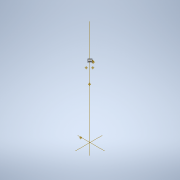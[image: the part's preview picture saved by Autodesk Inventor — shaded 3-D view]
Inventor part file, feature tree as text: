
AUTODESK INVENTOR PART (.ipt)
format: ipt  version: 2021 (Build 250183000, 183)  size: 13,105,664 bytes
history: native  units: mm
features: sketch x88, fillet x71, extrude x63, other x21, plane x15, revolve x12, pattern_circular x10, sweep x6, mirror x2, chamfer x1
ambient origin geometry x8: Origin, YZ Plane, XZ Plane, XY Plane, X Axis, Y Axis, Z Axis, Center Point
bodies: Body1 (feature_tree), Body2 (feature_tree), Body3 (feature_tree), Body4 (feature_tree), Body5 (feature_tree), Body6 (feature_tree), Body7 (feature_tree), Body8 (feature_tree), Body9 (feature_tree), Body10 (feature_tree), Body11 (feature_tree), Body12 (feature_tree)
feature tree (289):
  other  "Soyuz Core Stage"
  extrude  "Core Airframe"  Depth=133.0mm TaperAngle=0.0deg
  extrude  "Vernier Housing"  Depth=3.4mm
  extrude  "Main Engine Extrude"  TaperAngle=0.0deg  [1 undecoded]
  extrude  "Main Engine Cut"  Depth=3.4mm
  extrude  "Vernier Nozzels"  Depth=3.4mm
  extrude  "Extrusion11"  Depth=3.4mm
  extrude  "Extrusion12"  Depth=5.5mm
  sweep  "Sweep1"
  sweep  "Booster Nosecone"
  extrude  "Extrusion16"  Depth=4.5mm
  plane  "Work Plane6"
  extrude  "Extrusion17"  Depth=4.5mm
  plane  "Work Plane5"
  extrude  "Extrusion18"  Depth=4.5mm
  fillet  "Fillet11"  Radius=4.5mm
  fillet  "Fillet12"  Radius=6.0mm
  fillet  "Fillet13"  Radius=2.0mm
  fillet  "Fillet14"  Radius=10.5mm
  extrude  "Booster Lock Extrusion"  Depth=2.0mm
  extrude  "Booster Lock Cut"  Depth=10.5mm
  other  "Work Point1"
  plane  "Work Plane1"
  sweep  "Sweep4"
  extrude  "Extrusion26"  TaperAngle=0.0deg  [1 undecoded]
  fillet  "Fillet16"  [1 undecoded]
  plane  "Work Plane4"
  other  "Work Point2"
  plane  "Work Plane2"
  extrude  "Extrusion27"  Depth=5.0mm
  extrude  "Extrusion28"  Depth=5.0mm
  extrude  "Extrusion29"  Depth=5.0mm
  fillet  "Fillet17"  [1 undecoded]
  fillet  "Fillet18"  [1 undecoded]
  fillet  "Fillet19"  [1 undecoded]
  extrude  "Extrusion30"  Depth=9.0mm
  fillet  "Fillet20"  Radius=28.0mm
  fillet  "Fillet21"  Radius=25.0mm
  fillet  "Fillet22"  [1 undecoded]
  extrude  "Extrusion31"  Depth=13.0mm
  extrude  "Extrusion32"  TaperAngle=0.0deg  [1 undecoded]
  extrude  "Extrusion33"  TaperAngle=0.0deg  [1 undecoded]
  extrude  "Extrusion34"  TaperAngle=0.0deg  [1 undecoded]
  fillet  "Fillet23"  [1 undecoded]
  fillet  "Fillet24"  Radius=17.0mm
  fillet  "Fillet25"  Radius=23.0mm
  fillet  "Fillet26"  [1 undecoded]
  extrude  "Extrusion35"  TaperAngle=0.0deg  [1 undecoded]
  extrude  "Extrusion36"  Depth=15.0mm
  extrude  "Extrusion50"  Depth=1.5mm
  fillet  "Fillet75"  [1 undecoded]
  extrude  "Extrusion51"  Depth=3.0mm TaperAngle=0.0deg
  extrude  "Extrusion52"  Depth=0.5mm TaperAngle=0.0deg
  other  "Work Point13"
  sketch  "Sketch86"  dims[d351=0.0mm]
  sweep  "Sweep6"
  revolve  "Revolution2"  [1 undecoded]
  pattern_circular  "Circular Pattern5"  [2 undecoded]
  mirror  "Mirror4"
  revolve  "Revolution3"  [1 undecoded]
  fillet  "Fillet76"  Radius=1.0mm
  fillet  "Fillet77"  Radius=6.0mm
  fillet  "Fillet78"  [1 undecoded]
  fillet  "Fillet79"  [1 undecoded]
  fillet  "Fillet80"  Radius=5.0mm
  fillet  "Fillet81"  Radius=2.0mm
  fillet  "Fillet82"  Radius=2.0mm
  fillet  "Fillet83"  [1 undecoded]
  fillet  "Fillet84"  Radius=10.0mm
  fillet  "Fillet85"  Radius=0.5mm
  fillet  "Fillet86"  Radius=3.0mm
  extrude  "Extrusion54"  Depth=1.0mm
  fillet  "Fillet91"  Radius=1.0mm
  fillet  "Fillet92"  Radius=28.0mm
  fillet  "Fillet93"  Radius=0.5mm
  pattern_circular  "Circular Pattern6"  [2 undecoded]
  plane  "Work Plane20"
  extrude  "Extrusion56"  TaperAngle=0.0deg  [1 undecoded]
  pattern_circular  "Circular Pattern8"  [2 undecoded]
  extrude  "Extrusion57"  TaperAngle=0.0deg  [1 undecoded]
  extrude  "Extrusion58"  Depth=0.5mm TaperAngle=0.0deg
  fillet  "Fillet94"  Radius=3.0mm
  extrude  "Extrusion59"  Depth=0.5mm
  fillet  "Fillet95"  Radius=0.1mm
  pattern_circular  "Circular Pattern9"  Count=2  [1 undecoded]
  extrude  "Extrusion60"  Depth=0.5mm TaperAngle=0.0deg
  fillet  "Fillet96"  [1 undecoded]
  extrude  "Extrusion61"  TaperAngle=0.0deg  [1 undecoded]
  fillet  "Fillet97"  [1 undecoded]
  extrude  "Extrusion62"  TaperAngle=0.0deg  [1 undecoded]
  pattern_circular  "Circular Pattern11"  [2 undecoded]
  fillet  "Fillet98"  [1 undecoded]
  extrude  "Extrusion63"  TaperAngle=0.0deg  [1 undecoded]
  fillet  "Fillet99"  [1 undecoded]
  fillet  "Fillet100"  [1 undecoded]
  extrude  "Extrusion64"  TaperAngle=0.0deg  [1 undecoded]
  extrude  "Extrusion65"  TaperAngle=0.0deg  [1 undecoded]
  extrude  "Extrusion66"  TaperAngle=0.0deg  [1 undecoded]
  extrude  "Extrusion67"  Depth=0.5mm
  fillet  "Fillet101"  Radius=12.5mm
  plane  "Work Plane24"
  extrude  "Extrusion68"  Depth=0.5mm
  fillet  "Fillet102"  Radius=12.5mm
  extrude  "Extrusion69"  TaperAngle=0.0deg  [1 undecoded]
  pattern_circular  "Circular Pattern12"  [2 undecoded]
  extrude  "Extrusion70"  TaperAngle=0.0deg  [1 undecoded]
  fillet  "Fillet103"  [1 undecoded]
  pattern_circular  "Circular Pattern13"  [2 undecoded]
  extrude  "Extrusion71"  TaperAngle=0.0deg  [1 undecoded]
  extrude  "Extrusion72"  TaperAngle=0.0deg  [1 undecoded]
  extrude  "Extrusion73"  TaperAngle=0.0deg  [1 undecoded]
  fillet  "Fillet105"  [1 undecoded]
  extrude  "Extrusion74"  TaperAngle=0.0deg  [1 undecoded]
  extrude  "Extrusion75"  TaperAngle=0.0deg  [1 undecoded]
  fillet  "Fillet106"  [1 undecoded]
  fillet  "Fillet107"  Radius=6.0mm
  other  "Work Point16"
  revolve  "Revolution6"  [1 undecoded]
  other  "Work Point17"
  plane  "Work Plane26"
  extrude  "Extrusion81"  Depth=0.5mm
  fillet  "Fillet114"  Radius=6.0mm
  fillet  "Fillet115"  [1 undecoded]
  fillet  "Fillet116"  [1 undecoded]
  fillet  "Fillet117"  Radius=5.0mm
  mirror  "Mirror6"
  sweep  "Sweep8"
  pattern_circular  "Circular Pattern14"  [2 undecoded]
  extrude  "Extrusion80"  Depth=0.5mm
  revolve  "Revolution5"  [1 undecoded]
  extrude  "Extrusion82"  Depth=1.0mm
  fillet  "Fillet118"  [1 undecoded]
  other  "Work Point18"
  plane  "Work Plane27"
  extrude  "Extrusion83"  Depth=0.5mm
  sweep  "Sweep9"
  revolve  "Revolution7"  [1 undecoded]
  revolve  "Revolution8"  [1 undecoded]
  revolve  "Revolution9"  [1 undecoded]
  revolve  "Revolution10"  [1 undecoded]
  fillet  "Fillet119"  Radius=0.781667mm
  fillet  "Fillet120"  Radius=2.5mm
  fillet  "Fillet121"  Radius=12.5mm
  fillet  "Fillet122"  Radius=12.5mm
  fillet  "Fillet123"  Radius=0.5mm
  fillet  "Fillet124"  [1 undecoded]
  plane  "Work Plane30"
  extrude  "Extrusion85"  Depth=0.5mm
  extrude  "Extrusion86"  Depth=0.5mm
  extrude  "Extrusion87"  Depth=0.5mm
  extrude  "Extrusion88"  TaperAngle=0.0deg  [1 undecoded]
  fillet  "Fillet125"  Radius=1.0mm
  fillet  "Fillet126"  Radius=1.377412mm
  fillet  "Fillet127"  Radius=1.377mm
  fillet  "Fillet128"  Radius=4.5mm
  extrude  "Extrusion89"  Depth=1.0mm
  extrude  "Extrusion90"  Depth=0.5mm TaperAngle=0.0deg
  fillet  "Fillet129"  Radius=4.5mm
  fillet  "Fillet130"  Radius=1.377mm
  fillet  "Fillet131"  Radius=1.0mm
  extrude  "Extrusion92"  Depth=0.5mm
  extrude  "Extrusion93"  Depth=0.5mm
  fillet  "Fillet134"  Radius=1.0mm
  fillet  "Fillet135"  Radius=0.5mm
  fillet  "Fillet136"  Radius=4.5mm
  fillet  "Fillet138"  Radius=1.377mm
  pattern_circular  "Circular Pattern15"  [2 undecoded]
  other  "Work Point19"
  plane  "Work Plane31"
  extrude  "Extrusion94"  Depth=0.5mm
  fillet  "Fillet139"  Radius=1.0mm
  revolve  "Revolution11"  [1 undecoded]
  chamfer  "Chamfer3"  Distance=0.5mm
  fillet  "Fillet140"  Radius=4.5mm
  fillet  "Fillet141"  Radius=4.5mm
  fillet  "Fillet142"  Radius=1.377mm
  plane  "Work Plane32"
  revolve  "Revolution12"  [1 undecoded]
  fillet  "Fillet143"  Radius=1.0mm
  pattern_circular  "Circular Pattern16"  [2 undecoded]
  fillet  "Fillet144"  Radius=0.5mm
  sketch  "Sketch1"  dims[d0=20.0mm d1=133.0mm d2=0.0mm]
  sketch  "Sketch4"  dims[d7=0.0mm d9=3.4mm]
  sketch  "Sketch5"  dims[d10=3.4mm d12=0.0mm]
  sketch  "Sketch6"  dims[d15=3.4mm d18=3.4mm]
  sketch  "Sketch7"  dims[d20=3.4mm d21=3.4mm]
  sketch  "Sketch14"  dims[d25=3.4mm d26=3.4mm]
  sketch  "Sketch15"  dims[d33=7.0mm d34=0.0mm d47=5.5mm]
  sketch  "Sketch16"  dims[d48=5.5mm d49=5.5mm]
  sketch  "Sketch20"  dims[d50=5.5mm d52=4.5mm]
  other  "Soyuz Booster"
  sketch  "Sketch27"  dims[d53=4.5mm d54=4.5mm]
  sketch  "Sketch28"  dims[d55=4.5mm d56=4.5mm]
  sketch  "Sketch29"  dims[d57=4.5mm d58=4.5mm d59=4.5mm d60=6.0mm d61=2.094395mm d62=2.0mm d63=10.5mm]
  sketch  "Sketch31"  dims[d64=2.0mm d65=2.0mm]
  sketch  "Sketch32"  dims[d66=2.0mm d67=10.5mm]
  sketch  "Sketch34"  dims[d68=10.5mm d69=10.5mm]
  sketch  "Sketch35"  dims[d70=0.0mm d71=0.0mm d72=0.0mm]
  sketch  "Sketch41"  dims[d83=0.0mm d85=9.0mm d86=-1.396263mm d156=28.0mm d160=25.0mm d161=0.0mm]
  sketch  "Sketch42"  dims[d166=13.0mm d167=13.0mm d168=13.0mm d171=13.0mm]
  sketch  "Sketch43"  dims[d174=27.0mm d175=0.0mm d177=0.0mm]
  sketch  "Sketch45"  dims[d178=0.0mm d179=0.0mm]
  sketch  "Sketch49"  dims[d180=38.0mm d181=1.658063mm d236=0.0mm d237=0.0mm d278=17.0mm d280=23.0mm d281=-0.610865mm d282=0.0mm]
  sketch  "Sketch50"  dims[d304=0.0mm d309=0.0mm]
  sketch  "Sketch51"  dims[d311=15.0mm d312=15.0mm]
  sketch  "Sketch52"  dims[d313=19.0mm d314=1.5mm d316=-2.356194mm d317=0.0mm]
  sketch  "Sketch53"  dims[d318=0.0mm d330=3.0mm d331=0.0mm]
  sketch  "Sketch54"  dims[d334=0.5mm d335=0.0mm d338=0.5mm d339=0.0mm]
  sketch  "Sketch55"  dims[d342=3.0mm d343=3.0mm]
  sketch  "Sketch56"  dims[d344=3.0mm d345=6.0mm]
  other  "Core Stage Part 2"
  sketch  "Sketch57"  dims[d346=1.2mm]
  sketch  "Sketch81"  dims[d347=1.2mm]
  sketch  "Sketch82"  dims[d348=1.2mm]
  sketch  "Sketch83"  dims[d349=1.2mm]
  other  "Interstage 1"
  sketch  "Sketch85"  dims[d350=0.0mm]
  other  "Srf3"
  sketch  "3D Sketch5"
  other  "Project to Surface5"
  sketch  "Sketch87"  dims[d352=0.0mm]
  other  "Project to Surface7"
  sketch  "Sketch88"  dims[d353=0.0mm]
  sketch  "Sketch89"  dims[d354=14.5mm]
  sketch  "Sketch91"  dims[d355=14.5mm]
  plane  "Work Plane19"
  sketch  "Sketch93"  dims[d356=14.5mm]
  sketch  "Sketch94"  dims[d357=14.5mm]
  other  "Interstage 2"
  sketch  "Sketch95"  dims[d358=11.5mm d359=1.745329mm]
  other  "2nd Stage"
  sketch  "Sketch96"  dims[d361=2.2mm]
  sketch  "Sketch97"  dims[d362=1.6mm]
  sketch  "Sketch98"  dims[d363=0.0mm]
  sketch  "Sketch100"  dims[d364=4.1mm d365=-1.745329mm]
  other  "Srf4"
  sketch  "Sketch103"  dims[d366=0.0mm]
  sketch  "Sketch104"  dims[d367=1.6mm]
  sketch  "Sketch105"  dims[d368=2.2mm]
  sketch  "Sketch107"  dims[d369=0.0mm]
  sketch  "Sketch108"  dims[d370=1.6mm]
  sketch  "Sketch109"  dims[d371=2.2mm]
  sketch  "Sketch111"  dims[d372=1.6mm]
  sketch  "Sketch112"  dims[d373=0.0mm]
  sketch  "Sketch113"  dims[d374=2.2mm]
  sketch  "Sketch114"  dims[d397=5.5mm d398=4.5mm d400=5.5mm d401=4.5mm d402=4.5mm d403=5.5mm d404=4.5mm d406=5.5mm d410=2.094395mm d411=6.0mm]
  sketch  "Sketch115"  dims[d412=5.0mm d413=0.0mm d414=5.0mm d415=0.0mm d416=0.0mm d417=5.0mm d418=0.0mm d419=5.0mm d421=-1.396263mm d422=9.0mm]
  sketch  "Sketch116"  dims[d423=0.0mm]
  other  "2nd Stage Part 2"
  sketch  "Sketch117"  dims[d424=0.0mm]
  sketch  "Sketch118"  dims[d425=0.0mm]
  sketch  "Sketch120"  dims[d426=0.0mm]
  sketch  "Sketch121"  dims[d427=9.0mm]
  sketch  "Sketch123"  dims[d428=9.0mm]
  sketch  "Sketch128"  dims[d429=9.0mm]
  sketch  "Sketch129"  dims[d430=9.0mm]
  other  "Fairing"
  sketch  "Sketch130"  dims[d431=6.0mm]
  sketch  "Sketch131"  dims[d432=0.0mm]
  sketch  "Sketch132"  dims[d446=1.396263mm d447=5.0mm]
  sketch  "Sketch134"  dims[d449=2.0mm]
  sketch  "Sketch135"  dims[d450=2.0mm]
  sketch  "Sketch139"  dims[d452=21.5mm]
  sketch  "Sketch140"  dims[d453=21.5mm]
  sketch  "Sketch141"  dims[d454=6.2mm]
  sketch  "Sketch142"  dims[d455=6.2mm]
  other  "Escape Tower"
  plane  "Work Plane28"
  plane  "Work Plane29"
  sketch  "Sketch144"  dims[d456=0.5mm]
  other  "Grid Fins"
  sketch  "Sketch145"  dims[d459=0.5mm]
  sketch  "Sketch146"  dims[d460=0.5mm]
  sketch  "Sketch147"  dims[d461=0.0mm]
  sketch  "Sketch149"  dims[d464=0.5mm]
  sketch  "Sketch150"  dims[d465=1.3mm]
  sketch  "Sketch152"  dims[d466=0.0mm]
  sketch  "Sketch153"  dims[d467=1.3mm]
  sketch  "Sketch154"  dims[d468=3.0mm]
  sketch  "Sketch156"  dims[d470=3.0mm]
  sketch  "Sketch157"  dims[d472=0.0mm d473=0.0mm d475=6.0mm d476=1.0mm d477=6.0mm d478=0.0mm d479=-0.202458mm d480=0.0mm d481=5.0mm d482=2.0mm d483=2.0mm d484=0.0mm d485=10.0mm d486=0.0mm d487=0.5mm d489=3.0mm d490=1.0mm d491=1.0mm d492=28.0mm d493=0.5mm d494=0.0mm d518=0.0mm d521=0.0mm d522=0.0mm d524=0.0mm d525=0.5mm d526=0.0mm d527=3.0mm d528=3.0mm d529=0.1mm d530=20.0mm d531=7.0mm d532=0.0mm d538=0.0mm d539=0.0mm d540=0.0mm d541=0.0mm d542=0.0mm d543=0.0mm d544=0.0mm d545=0.0mm d546=0.0mm d547=0.0mm d548=0.0mm d549=0.0mm d550=12.5mm d551=12.5mm d553=12.5mm d554=12.5mm d556=0.0mm d557=0.0mm d561=0.0mm d562=0.0mm d563=0.0mm d564=0.0mm d566=0.0mm d567=0.0mm d568=0.0mm d571=0.0mm d572=0.0mm d573=0.0mm d575=6.0mm d576=6.0mm d577=6.0mm d578=6.0mm d579=0.0mm d581=0.0mm d582=5.0mm d583=-6.108652mm d584=1.0mm d585=1.0mm d593=2.0mm d594=3.0mm d604=1.0mm d608=0.0mm d609=2.0mm d610=0.0mm d611=3.0mm d612=1.0mm d614=0.0mm d617=1.0mm d618=0.781667mm d619=2.5mm d649=12.5mm d650=12.5mm d651=0.5mm d652=0.0mm d653=0.5mm d654=4.5mm d655=4.5mm d657=0.0mm d658=1.0mm d659=1.377412mm d660=1.377mm d661=4.5mm d662=1.0mm d663=0.5mm d664=0.0mm d665=4.5mm d666=1.377mm d667=1.0mm d668=4.5mm d669=1.377mm d670=1.0mm d671=0.5mm d672=0.0mm d673=4.5mm d674=1.377mm d675=4.5mm d676=1.377mm d677=1.0mm d678=1.0mm d679=0.5mm d680=0.0mm d681=4.5mm d682=4.5mm d683=1.377mm d684=1.377mm d685=1.0mm d686=1.0mm d687=0.5mm d688=0.0mm d689=0.5mm d690=0.2mm d691=0.3mm d692=1.0mm d694=0.0mm d695=0.0mm d696=0.1mm d697=5.0mm d698=0.0mm d699=0.0mm d700=0.0mm d702=50.0mm d703=-0.541052mm d709=0.0mm d993=0.0mm d994=0.0mm d995=2.5mm d996=5.0mm d997=0.0mm d998=8.0mm d999=0.0mm d1000=0.0mm d1001=0.0mm d1002=0.0mm d1003=0.0mm d1004=0.0mm d1005=4.0mm d1006=0.0mm d1007=0.0mm d1008=0.0mm d1009=0.0mm d1010=0.0mm d1011=0.0mm d1012=0.0mm d1013=4.1mm d1014=0.0mm d1026=45.0deg d1030=0.0mm d1031=0.0mm d1034=10.0mm d1035=3.0mm d1036=0.0mm d1037=0.0mm d1038=0.1mm d1039=0.0mm d1040=2.5mm d1041=2.5mm d1042=0.9mm d1048=2.5mm d1049=2.6mm d1050=90.0deg d1051=60.0mm d1052=360.0deg d1054=1.5mm d1057=0.4mm d1058=90.0deg d1059=0.2mm d1060=0.7mm d1061=0.4mm d1062=1.0mm d1063=0.5mm d1064=0.2mm d1065=0.2mm d1066=0.2mm d1067=0.2mm d1068=0.2mm d1069=0.2mm d1070=0.1mm d1083=0.5mm d1084=0.3mm d1085=2.0mm d1086=0.0mm d1087=1.3mm d1088=0.0mm d1089=0.7mm d1090=0.5mm d1091=0.7mm d1092=60.0mm d1093=360.0deg d1103=-1.0mm d1104=0.0mm d1105=0.0mm d1106=0.0mm d1107=0.0mm d1108=30.0mm d1109=1.25mm d1110=1.4mm d1111=0.0mm d1112=1.25mm d1116=40.0mm d1117=360.0deg d1119=0.0mm d1120=0.0mm d1121=0.0mm d1122=0.0mm d1123=0.0mm d1124=0.0mm d1125=16.0mm d1126=0.0mm d1127=0.0mm d1128=0.0mm d1129=0.0mm d1130=30.0mm d1131=0.0mm d1132=0.1mm d1133=1.7mm d1134=14.0mm d1135=5.0mm d1136=0.0mm d1137=0.8mm d1138=60.0mm d1139=360.0deg d1141=0.0mm d1142=3.0mm d1143=0.0mm d1144=0.5mm d1145=1.0mm d1146=6.0mm d1147=0.0mm d1148=8.0mm d1149=0.0mm d1150=3.0mm d1151=9.0mm d1152=6.981317mm d1153=9.6mm d1154=90.0deg d1193=3.5mm d1194=1.2mm d1195=0.0mm d1196=2.5mm d1197=1.8mm d1200=2.0mm d1201=10.0mm d1203=0.3mm d1204=0.2mm d1205=9.397169mm d1206=1.165699mm d1207=1.2mm d1208=2.0mm d1209=2.0mm d1210=0.0mm d1211=60.0mm d1212=360.0deg d1214=8.0mm d1215=0.0mm d1216=0.0mm d1217=20.0mm d1218=2.0mm d1219=0.0mm d1220=0.2mm d1221=0.2mm d1222=5.5mm d1223=4.5mm d1224=4.5mm d1228=5.0mm d1229=4.0mm d1230=2.094395mm d1231=-2.094395mm d1232=0.0mm d1233=0.0mm d1234=0.0mm d1235=5.0mm d1236=4.014257mm d1238=0.0mm d1239=0.0mm d1240=1.5mm d1241=10.5mm d1242=-1.396263mm d1243=2.0mm d1244=8.5mm d1245=0.0mm d1246=4.0mm d1247=1.745329mm d1248=0.8mm d1249=1.5mm d1250=3.0mm d1251=8.5mm d1252=2.8mm d1253=0.0mm d1254=1.4mm d1258=6.8mm d1259=0.872665mm d1260=0.0mm d1261=0.0mm d1262=0.0mm d1263=0.0mm d1264=0.55mm d1265=0.0mm d1266=40.0mm d1267=360.0deg d1270=0.0mm d1271=0.0mm d1272=0.0mm d1273=3.55mm d1274=0.0mm d1275=0.8mm d1276=60.0mm d1277=360.0deg d1282=20.0mm d1283=0.349066mm d1286=4.0mm d1287=0.0mm d1288=0.2mm d1289=1.0mm d1290=0.0mm d1291=0.2mm d1292=3.5mm d1293=5.0mm d1294=7.0mm d1295=0.0mm d1296=5.0mm d1297=5.0mm d1298=0.0mm d1299=1.0mm d1300=1.0mm d1310=0.0mm d1311=0.0mm d1313=11.5mm d1316=0.3mm d1317=0.3mm d1318=3.066164mm d1319=2.367748mm d1320=9.41mm d1321=4.705mm d1324=1.81mm d1330=0.0mm d1331=0.0mm d1333=3.0mm d1361=20.0mm d1362=360.0deg d1372=0.0mm d1375=0.0mm d1391=1.0mm d1392=1.3mm d1393=2.0mm d1394=2.0mm d1395=2.0mm d1396=2.0mm d1397=1.0mm d1398=1.0mm d1399=1.0mm d1400=1.0mm d1401=1.0mm d1402=1.0mm d1403=13.566164mm d1404=12.266164mm d1405=13.566164mm d1406=12.266164mm d1407=13.566164mm d1408=12.266164mm d1409=13.566164mm d1410=12.266164mm d1411=2.0mm d1412=90.0deg d1413=1.2mm d1414=2.5mm d1417=3.0mm d1418=0.0mm d1424=3.0mm d1425=15.53343mm d1429=180.0deg d1430=23.0mm d1431=12.2mm d1432=45.0deg d1433=2.5mm d1434=2.5mm d1435=3.4mm d1436=3.4mm d1437=0.0mm d1438=0.0mm d1439=1.3mm d1440=0.0mm d1441=0.5mm d1442=0.4mm d1443=0.4mm d1444=0.4mm d1445=11.586164mm d1446=0.0mm d1447=0.0mm d1448=0.0mm d1449=0.0mm d1452=0.0mm d1453=1.3mm d1454=0.0mm d1455=0.0mm d1456=0.0mm d1458=13.566164mm d1459=12.266164mm d1460=12.266164mm d1461=13.566164mm d1462=2.0mm d1463=1.5mm d1464=0.0mm d1465=0.1mm d1469=5.0mm d1470=5.0mm d1471=20.0mm d1473=1.071mm d1474=0.0mm d1475=0.0mm d1476=0.0mm d1477=0.0mm d1478=0.0mm d1479=0.0mm d1482=19.3mm d1483=0.0mm d1484=16.057029mm d1485=3.0mm d1486=0.0mm d1487=0.0mm d1490=0.0mm d1497=15.184364mm d1498=15.0mm d1499=180.0deg d1500=27.0mm d1501=15.620697mm d1502=180.0deg d1504=60.0deg d1513=13.856406mm d1514=180.0deg d1528=14.0mm d1529=3.579724mm d1531=1.0mm d1532=1.000457mm d1533=0.917096mm d1534=1.0mm d1540=2.0mm d1541=1.329428mm d1543=1.5mm d1545=4.997278mm d1546=0.0mm d1547=3.0mm d1552=2.7mm d1554=30.892328mm d1555=2.0mm d1556=3.250296mm d1557=6.497278mm d1560=0.0mm d1561=21.46755mm d1562=25.0mm d1563=1.5mm d1564=0.0mm d1566=20.071286mm d1567=37.0mm d1568=1.0mm d1569=1.0mm d1570=27.0mm d1571=45.0mm d1572=90.0deg d1574=0.917096mm d1575=0.4mm d1576=0.4mm d1577=0.4mm d1578=0.1mm d1579=0.1mm d1580=0.2mm d1583=2.0mm d1593=1.0mm d1594=1.0mm d1596=0.5mm d1597=2.5mm d1598=3.5mm d1599=3.5mm d1600=3.5mm d1601=2.0mm d1602=0.0mm d1603=0.7mm d1604=0.7mm d1605=4.0mm d1606=0.7mm d1607=0.7mm d1608=0.0mm d1609=0.0mm d1610=0.0mm d1611=0.0mm d1612=0.0mm d1613=0.3mm d1614=0.0mm d1615=0.2mm d1616=2.0mm d1617=1.0mm d1618=2.0mm d1619=1.0mm d1621=100.0mm d1622=2.0mm d1623=2.0mm d1624=2.0mm d1625=0.0mm d1626=0.0mm d1627=0.9mm d1628=0.1mm d1629=0.1mm d1630=0.1mm d1632=1.0mm d1633=0.75mm d1634=0.75mm d1635=0.0mm d1636=0.0mm d1640=7.0mm d1641=7.0mm d1642=3.5mm d1643=0.7mm d1644=6.0mm d1645=0.0mm d1646=2.0mm d1649=0.0mm d1650=2.0mm d1651=2.25mm d1652=4.5mm d1653=0.0mm d1654=0.0mm d1655=4.0mm d1656=1.0mm d1657=0.5mm d1667=1.0mm d1668=0.0mm d1669=0.0mm d1670=0.0mm d1674=0.8mm d1676=0.8mm d1677=0.5mm d1678=0.5mm d1679=1.5mm d1680=1.7mm d1681=0.0mm d1682=2.0mm d1683=0.2mm d1684=0.1mm d1686=0.1mm d1687=20.0mm d1688=90.0deg d1690=3.5mm d1691=0.0mm d1692=4.5mm d1693=4.5mm d1694=0.0mm d1695=2.0mm d1696=0.0mm d1697=1.0mm d1698=4.0mm d1699=2.0mm d1700=45.0deg d1701=12.0mm d1702=3.0mm d1703=10.7mm d1705=5.0mm d1706=12.0mm d1707=2.443461mm d1708=1.0mm d1709=2.0mm d1710=45.0deg d1711=0.5mm d1712=0.5mm d1713=0.5mm d1714=4.5mm d1715=5.5mm d1716=8.0mm d1717=8.5mm d1718=9.424778mm d1719=3.3mm d1720=2.3mm d1721=1.745329mm d1722=0.5mm d1723=20.0mm d1724=19.198622mm d1726=0.5mm d1731=0.5mm d1732=0.5mm d1733=0.5mm d1734=0.5mm d1735=0.5mm d1736=0.5mm d1737=0.5mm d1738=0.5mm d1739=0.5mm d1740=0.5mm d1741=0.5mm d1742=0.5mm d1743=0.5mm d1744=0.5mm d1745=0.5mm d1746=0.5mm d1747=0.5mm d1748=0.5mm d1749=0.5mm d1755=0.5mm d1756=0.5mm d1757=0.5mm d1758=0.5mm d1759=0.5mm d1760=0.5mm d1763=0.5mm d1764=0.5mm d1766=0.5mm d1767=0.5mm d1768=0.5mm d1769=0.5mm d1770=0.5mm d1771=0.5mm d1772=0.5mm d1773=0.5mm d1774=0.5mm d1775=0.5mm d1776=0.5mm d1777=0.5mm d1778=0.5mm d1779=0.5mm d1780=0.5mm d1781=0.5mm d1782=0.5mm d1783=0.5mm d1784=0.5mm d1785=0.5mm d1786=0.5mm d1787=0.5mm d1788=0.5mm d1789=0.5mm d1790=0.5mm d1791=0.5mm d1792=0.5mm d1793=0.5mm d194=0.5mm d195=0.872665mm d196=0.5mm d197=0.872665mm d261=0.5mm d262=0.872665mm d263=0.5mm d264=0.872665mm d808=0.5mm d809=0.872665mm d810=0.5mm d811=0.872665mm d1255=0.872665mm d1351=0.5mm d1352=0.872665mm d1353=0.5mm d1354=0.872665mm]
  extrude  "Extrusion23"  Depth=0.5mm
  extrude  "Extrusion24"  Depth=0.2mm
  extrude  "Extrusion25"  Depth=0.5mm
  revolve  "RevolutionSrf2"  [1 undecoded]
  revolve  "RevolutionSrf3"  [1 undecoded]
  sketch  "Sketch38"  dims[d73=0.0mm d74=5.0mm d75=1.396263mm]
  sketch  "Sketch39"  dims[d76=5.0mm d77=5.0mm]
  sketch  "Sketch40"  dims[d78=5.0mm d79=5.0mm d80=0.0mm d81=0.0mm d82=0.0mm]
note: 76 required parameter values undecoded (feature->parameter linkage not recoverable at this tier; creation-order binding heuristic only, values carry confidence <= 0.55)